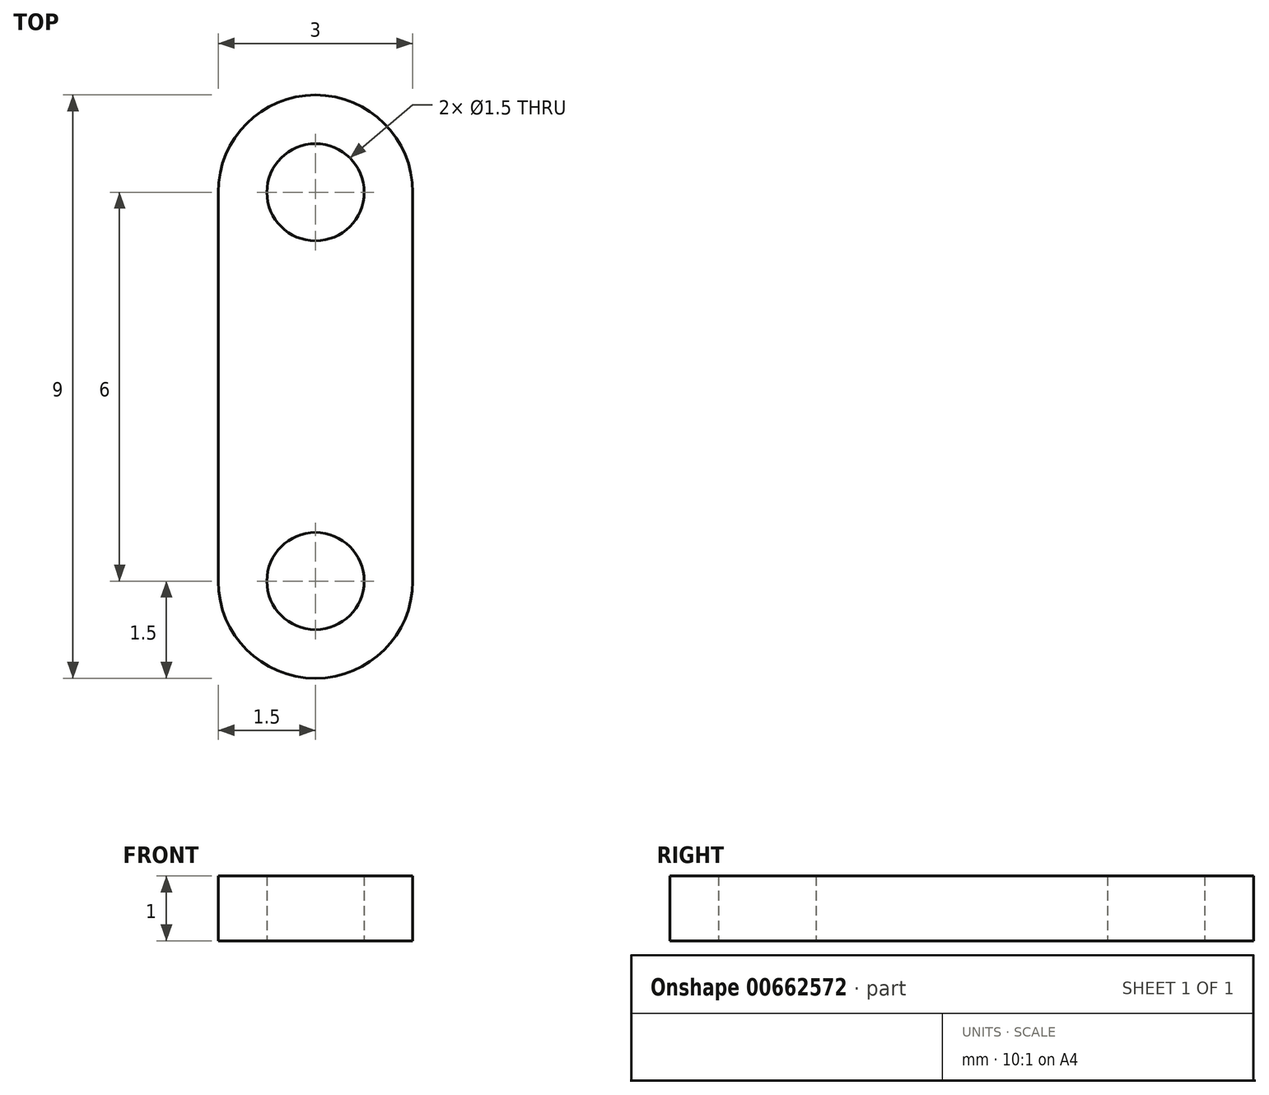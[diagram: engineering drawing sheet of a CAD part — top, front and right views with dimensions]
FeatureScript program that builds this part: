
annotation { "Feature Type Name" : "Feature", "Feature Type Description" : "" }
export const myFeature = defineFeature(function(context is Context, id is Id, definition is map)
    precondition{}
    {
        {
            var Q0;
            Q0=qCreatedBy(makeId("Top.planeOp"),FACE);
            var sketch = newSketch(context, id + "F0", { "sketchPlane" : qUnion([Q0])});
            skLineSegment(sketch, "E0", {"start": v(0, 0) * mm, "end": v(0, 3) * mm});
            skLineSegment(sketch, "E1", {"start": v(3, 3) * mm, "end": v(3, 0) * mm});
            skArc(sketch, "E2", {"start": v(3, 3) * mm, "mid": v(1.5, 4.5) * mm, "end": v(0, 3) * mm});
            skCircle(sketch, "E3", {"center": v(1.5, 3) * mm, "radius": 0.75 * mm});
            skLineSegment(sketch, "E4.MirrorCS", {"start": v(3, -3) * mm, "end": v(3, 0) * mm});
            skLineSegment(sketch, "E5.MirrorCS", {"start": v(0, 0) * mm, "end": v(0, -3) * mm});
            skCircle(sketch, "E6.MirrorC", {"center": v(1.5, -3) * mm, "radius": 0.75 * mm});
            skArc(sketch, "E7.MirrorCS", {"start": v(3, -3) * mm, "mid": v(1.5, -4.5) * mm, "end": v(0, -3) * mm});
            skSolve(sketch);
        }
        {
            var Q0;
            Q0=makeQuery(id+"F0.imprint","IMPRINT",FACE,{"disambiguationData":[TD([[makeQuery(id+"F0.imprint","IMPRINT",EDGE,{"derivedFrom":sQuery(id+"F0.wireOp",EDGE,"E0")}),-1.0]])]});
            extrude(context, id + "F1", {"entities" : qUnion([Q0]), "depth" : 1 * mm, "offsetDistance" : 25 * mm});
        }
    });
